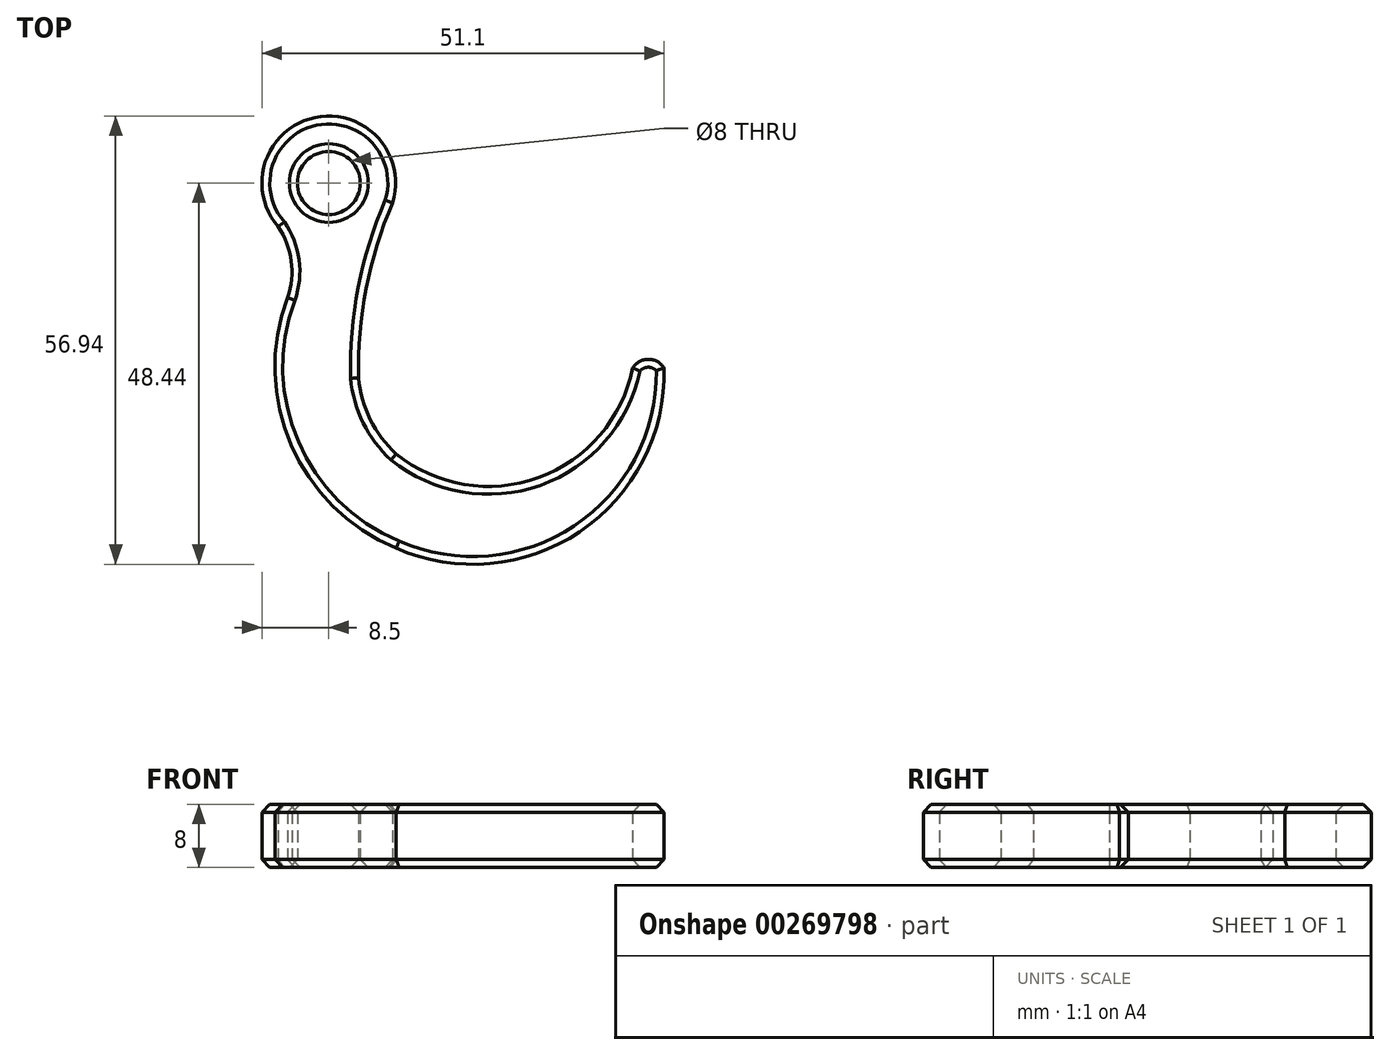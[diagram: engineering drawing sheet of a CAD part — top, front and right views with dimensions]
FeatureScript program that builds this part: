
annotation { "Feature Type Name" : "Feature", "Feature Type Description" : "" }
export const myFeature = defineFeature(function(context is Context, id is Id, definition is map)
    precondition{}
    {
        {
            var Q0;
            Q0=qCreatedBy(makeId("Top.planeOp"),FACE);
            var sketch = newSketch(context, id + "F0", { "sketchPlane" : qUnion([Q0])});
            skArc(sketch, "E0", {"start": v(7.5, -3.98) * mm, "mid": v(-0.95, 8.45) * mm, "end": v(-6.44, -5.55) * mm});
            skCircle(sketch, "E1", {"center": v(0, 0) * mm, "radius": 4 * mm});
            skLineSegment(sketch, "E2", {"start": v(0, 0) * mm, "end": v(8.55, -23.5) * mm, "construction": true});
            skArc(sketch, "E3", {"start": v(5.15, -11.46) * mm, "mid": v(4.71, -11.6) * mm, "end": v(4.28, -11.75) * mm});
            skArc(sketch, "E4", {"start": v(-5.25, -14.55) * mm, "mid": v(-4.77, -9.9) * mm, "end": v(-6.44, -5.55) * mm});
            skArc(sketch, "E5", {"start": v(8.12, -2.53) * mm, "mid": v(4.73, -13.4) * mm, "end": v(3.76, -24.76) * mm});
            skArc(sketch, "E6", {"start": v(-5.25, -14.55) * mm, "mid": v(-4.79, -33.26) * mm, "end": v(8.55, -46.4) * mm});
            skArc(sketch, "E7", {"start": v(8.55, -46.4) * mm, "mid": v(31.87, -44.3) * mm, "end": v(42.6, -23.5) * mm});
            skArc(sketch, "E8", {"start": v(42.6, -23.5) * mm, "mid": v(40.6, -22.4) * mm, "end": v(38.6, -23.5) * mm});
            skArc(sketch, "E9", {"start": v(8.55, -34.42) * mm, "mid": v(26.65, -37.42) * mm, "end": v(38.6, -23.5) * mm});
            skArc(sketch, "E10", {"start": v(3.76, -24.76) * mm, "mid": v(5.26, -30.03) * mm, "end": v(8.55, -34.42) * mm});
            skSolve(sketch);
        }
        {
            var Q0;
            Q0=makeQuery(id+"F0.imprint","IMPRINT",FACE,{"disambiguationData":[TD([[makeQuery(id+"F0.imprint","IMPRINT",EDGE,{"derivedFrom":sQuery(id+"F0.wireOp",EDGE,"E1")}),-1.0]])]});
            extrude(context, id + "F1", {"entities" : qUnion([Q0]), "offsetDistance" : 25 * mm, "depth" : 8 * mm});
        }
        {
            var Q0;
            Q0=makeQuery(id+"F1.opExtrude","CAP_EDGE",EDGE,{"disambiguationData":[OSD([sQuery(id+"F0.wireOp",EDGE,"WmjTHoMl-QORS-I3cK-UAXQ-Y7lYyYcCy2qp")])],"isStart":true});
            var Q1;
            Q1=makeQuery(id+"F1.opExtrude","CAP_EDGE",EDGE,{"disambiguationData":[OSD([sQuery(id+"F0.wireOp",EDGE,"c3d705f9-ca42-4a88-84ab-0556390c2014")])],"isStart":true});
            var Q2;
            Q2=makeQuery(id+"F1.opExtrude","CAP_EDGE",EDGE,{"disambiguationData":[OSD([sQuery(id+"F0.wireOp",EDGE,"hgBG9bT5-cQhy-xP4Q-mzdk-DAOOgwEgxOIi")])],"isStart":true});
            var Q3;
            Q3=makeQuery(id+"F1.opExtrude","CAP_EDGE",EDGE,{"disambiguationData":[OSD([sQuery(id+"F0.wireOp",EDGE,"YPu4BJlP-wECV-bRLm-omAV-OikBBG63YrVU")])],"isStart":true});
            var Q4;
            Q4=makeQuery(id+"F1.opExtrude","CAP_EDGE",EDGE,{"disambiguationData":[OSD([sQuery(id+"F0.wireOp",EDGE,"5e23f0a8-8a0e-45a9-a401-5ad86917c9f1.trimOffspring")])],"isStart":true});
            var Q5;
            Q5=makeQuery(id+"F1.opExtrude","CAP_EDGE",EDGE,{"disambiguationData":[OSD([sQuery(id+"F0.wireOp",EDGE,"E4")])],"isStart":true});
            var Q6;
            Q6=makeQuery(id+"F1.opExtrude","CAP_EDGE",EDGE,{"disambiguationData":[OSD([sQuery(id+"F0.wireOp",EDGE,"E5")])],"isStart":true});
            var Q7;
            Q7=makeQuery(id+"F1.opExtrude","CAP_EDGE",EDGE,{"disambiguationData":[OSD([sQuery(id+"F0.wireOp",EDGE,"E0")])],"isStart":true});
            var Q8;
            Q8=makeQuery(id+"F1.opExtrude","CAP_EDGE",EDGE,{"disambiguationData":[OSD([sQuery(id+"F0.wireOp",EDGE,"acd212bc-6ee3-4b6d-9d7e-a0b89d02b1fb")])],"isStart":true});
            var Q9;
            Q9=makeQuery(id+"F1.opExtrude","CAP_EDGE",EDGE,{"disambiguationData":[OSD([sQuery(id+"F0.wireOp",EDGE,"E1")])],"isStart":true});
            var Q10;
            Q10=makeQuery(id+"F1.opExtrude","CAP_EDGE",EDGE,{"disambiguationData":[OSD([sQuery(id+"F0.wireOp",EDGE,"5e23f0a8-8a0e-45a9-a401-5ad86917c9f1.trimOffspring")])],"isStart":false});
            var Q11;
            Q11=makeQuery(id+"F1.opExtrude","CAP_EDGE",EDGE,{"disambiguationData":[OSD([sQuery(id+"F0.wireOp",EDGE,"E4")])],"isStart":false});
            var Q12;
            Q12=makeQuery(id+"F1.opExtrude","CAP_EDGE",EDGE,{"disambiguationData":[OSD([sQuery(id+"F0.wireOp",EDGE,"E0")])],"isStart":false});
            var Q13;
            Q13=makeQuery(id+"F1.opExtrude","CAP_EDGE",EDGE,{"disambiguationData":[OSD([sQuery(id+"F0.wireOp",EDGE,"E5")])],"isStart":false});
            var Q14;
            {var subQ0=sQuery(id+"F0.wireOp",EDGE,"9hyJGXkA-CCMY-FrrT-r3Id-dfKAuHx7PUYm");var subQ1=sQuery(id+"F0.wireOp",EDGE,"acd212bc-6ee3-4b6d-9d7e-a0b89d02b1fb");Q14=makeQuery(id+"FD3D7Fteemorltv_1.opFillet","BLEND_EDGE",EDGE,{"blendedFrom":[makeQuery(id+"F1.opExtrude","SWEPT_EDGE",EDGE,{"disambiguationData":[OSD([subQ1,subQ0])]}),makeQuery(id+"F1.opExtrude","CAP_FACE",FACE,{"disambiguationData":[OSD([sQuery(id+"F0.wireOp",EDGE,"E0"),sQuery(id+"F0.wireOp",EDGE,"E1"),sQuery(id+"F0.wireOp",EDGE,"YPu4BJlP-wECV-bRLm-omAV-OikBBG63YrVU"),sQuery(id+"F0.wireOp",EDGE,"E4"),sQuery(id+"F0.wireOp",EDGE,"E5"),sQuery(id+"F0.wireOp",EDGE,"hgBG9bT5-cQhy-xP4Q-mzdk-DAOOgwEgxOIi"),sQuery(id+"F0.wireOp",EDGE,"5e23f0a8-8a0e-45a9-a401-5ad86917c9f1.trimOffspring"),subQ1,subQ0])],"isStart":false})],"blendedInto":[makeQuery(id+"F1.opExtrude","CAP_FACE",FACE,{"disambiguationData":[OSD([sQuery(id+"F0.wireOp",EDGE,"E0"),sQuery(id+"F0.wireOp",EDGE,"E1"),sQuery(id+"F0.wireOp",EDGE,"YPu4BJlP-wECV-bRLm-omAV-OikBBG63YrVU"),sQuery(id+"F0.wireOp",EDGE,"E4"),sQuery(id+"F0.wireOp",EDGE,"E5"),sQuery(id+"F0.wireOp",EDGE,"hgBG9bT5-cQhy-xP4Q-mzdk-DAOOgwEgxOIi"),sQuery(id+"F0.wireOp",EDGE,"5e23f0a8-8a0e-45a9-a401-5ad86917c9f1.trimOffspring"),subQ1,subQ0])],"isStart":false})]});}
            var Q15;
            Q15=makeQuery(id+"F1.opExtrude","CAP_EDGE",EDGE,{"disambiguationData":[OSD([sQuery(id+"F0.wireOp",EDGE,"E1")])],"isStart":false});
            var Q16;
            Q16=makeQuery(id+"F1.opExtrude","CAP_EDGE",EDGE,{"disambiguationData":[OSD([sQuery(id+"F0.wireOp",EDGE,"E9")])],"isStart":false});
            var Q17;
            Q17=makeQuery(id+"F1.opExtrude","CAP_EDGE",EDGE,{"disambiguationData":[OSD([sQuery(id+"F0.wireOp",EDGE,"E9")])],"isStart":true});
            var Q18;
            Q18=makeQuery(id+"F1.opExtrude","CAP_EDGE",EDGE,{"disambiguationData":[OSD([sQuery(id+"F0.wireOp",EDGE,"E7")])],"isStart":true});
            var Q19;
            Q19=makeQuery(id+"F1.opExtrude","CAP_EDGE",EDGE,{"disambiguationData":[OSD([sQuery(id+"F0.wireOp",EDGE,"E7")])],"isStart":false});
            var Q20;
            Q20=makeQuery(id+"F1.opExtrude","CAP_EDGE",EDGE,{"disambiguationData":[OSD([sQuery(id+"F0.wireOp",EDGE,"E8")])],"isStart":false});
            var Q21;
            Q21=makeQuery(id+"F1.opExtrude","CAP_EDGE",EDGE,{"disambiguationData":[OSD([sQuery(id+"F0.wireOp",EDGE,"E8")])],"isStart":true});
            chamfer(context, id + "F2", {"entities" : qUnion([Q0, Q1, Q2, Q3, Q4, Q5, Q6, Q7, Q8, Q9, Q10, Q11, Q12, Q13, Q14, Q15, Q16, Q17, Q18, Q19, Q20, Q21]), "width" : 1 * mm, "tangentPropagation" : true});
        }
    });
